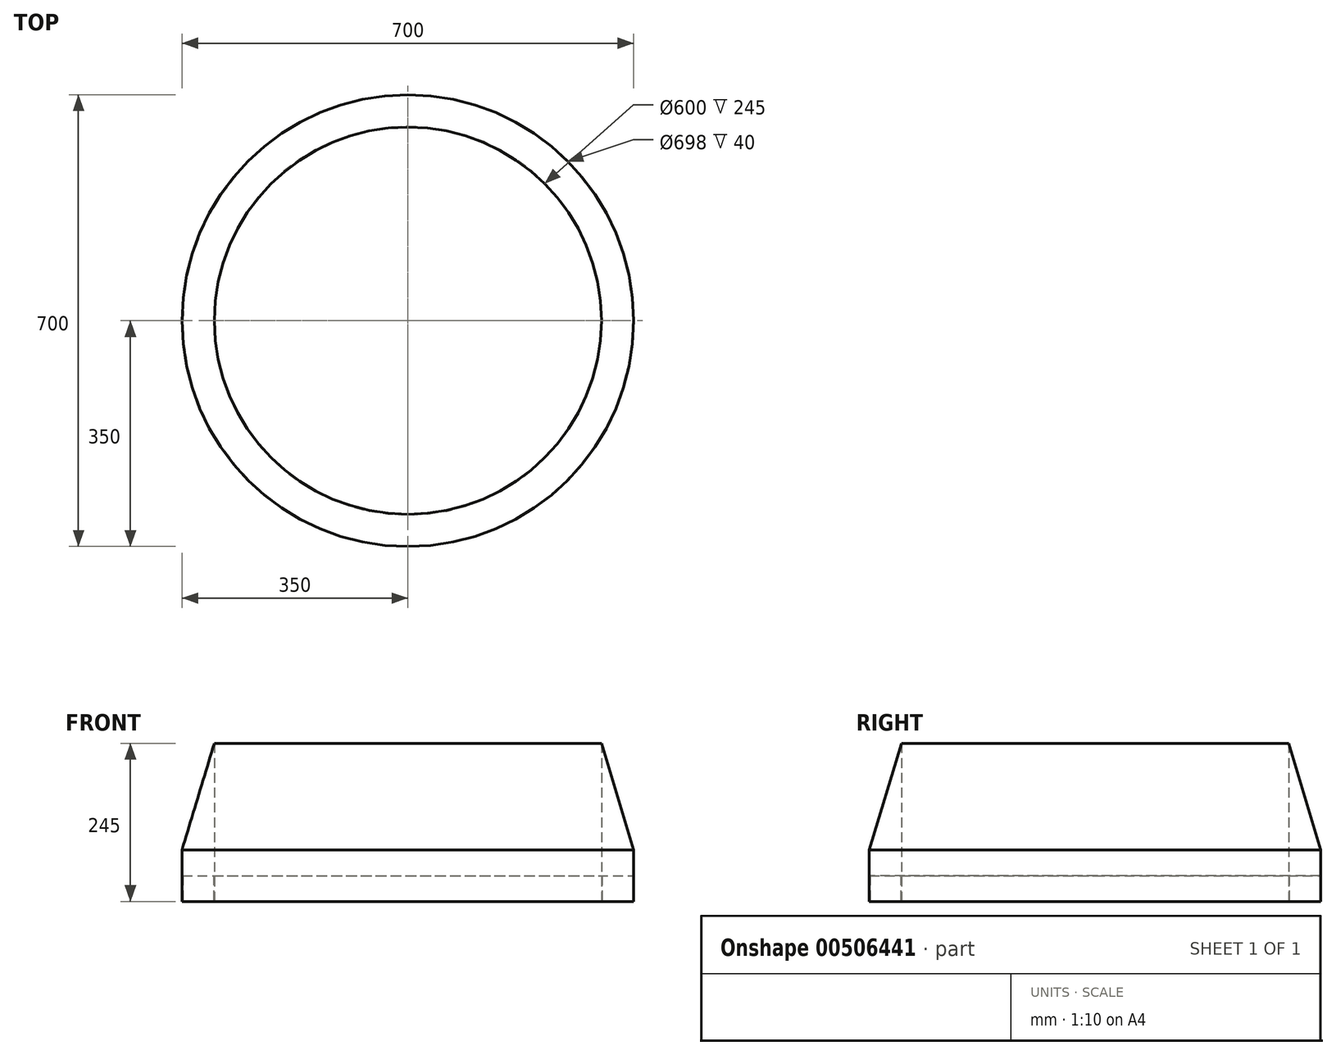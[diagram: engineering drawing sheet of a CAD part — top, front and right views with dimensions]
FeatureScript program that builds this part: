
annotation { "Feature Type Name" : "Feature", "Feature Type Description" : "" }
export const myFeature = defineFeature(function(context is Context, id is Id, definition is map)
    precondition{}
    {
        {
            var Q0;
            Q0=qCreatedBy(makeId("Front.planeOp"),FACE);
            var sketch = newSketch(context, id + "F0", { "sketchPlane" : qUnion([Q0])});
            skLineSegment(sketch, "E0", {"start": v(0, -139.25) * mm, "end": v(0, 240.83) * mm, "construction": true});
            skLineSegment(sketch, "E1", {"start": v(-300, -67.22) * mm, "end": v(-300, 177.78) * mm});
            skLineSegment(sketch, "E2", {"start": v(-300, 177.78) * mm, "end": v(-350, 12.78) * mm});
            skLineSegment(sketch, "E3", {"start": v(-350, 12.78) * mm, "end": v(-350, -67.22) * mm});
            skLineSegment(sketch, "E4", {"start": v(-350, -67.22) * mm, "end": v(-349, -67.22) * mm});
            skLineSegment(sketch, "E5", {"start": v(-349, -67.22) * mm, "end": v(-349, -27.22) * mm});
            skLineSegment(sketch, "E6", {"start": v(-349, -27.22) * mm, "end": v(-301, -27.22) * mm});
            skLineSegment(sketch, "E7", {"start": v(-301, -27.22) * mm, "end": v(-301, -67.22) * mm});
            skLineSegment(sketch, "E8", {"start": v(-301, -67.22) * mm, "end": v(-300, -67.22) * mm});
            skSolve(sketch);
        }
        {
            var Q0;
            Q0=qSketchRegion(id+"F0",true);
            var Q1;
            Q1=sQuery(id+"F0.wireOp",EDGE,"E0");
            revolve(context, id + "F1", {"entities" : qUnion([Q0]), "axis" : qUnion([Q1]), "revolveType" : RevolveType.FULL});
        }
    });
